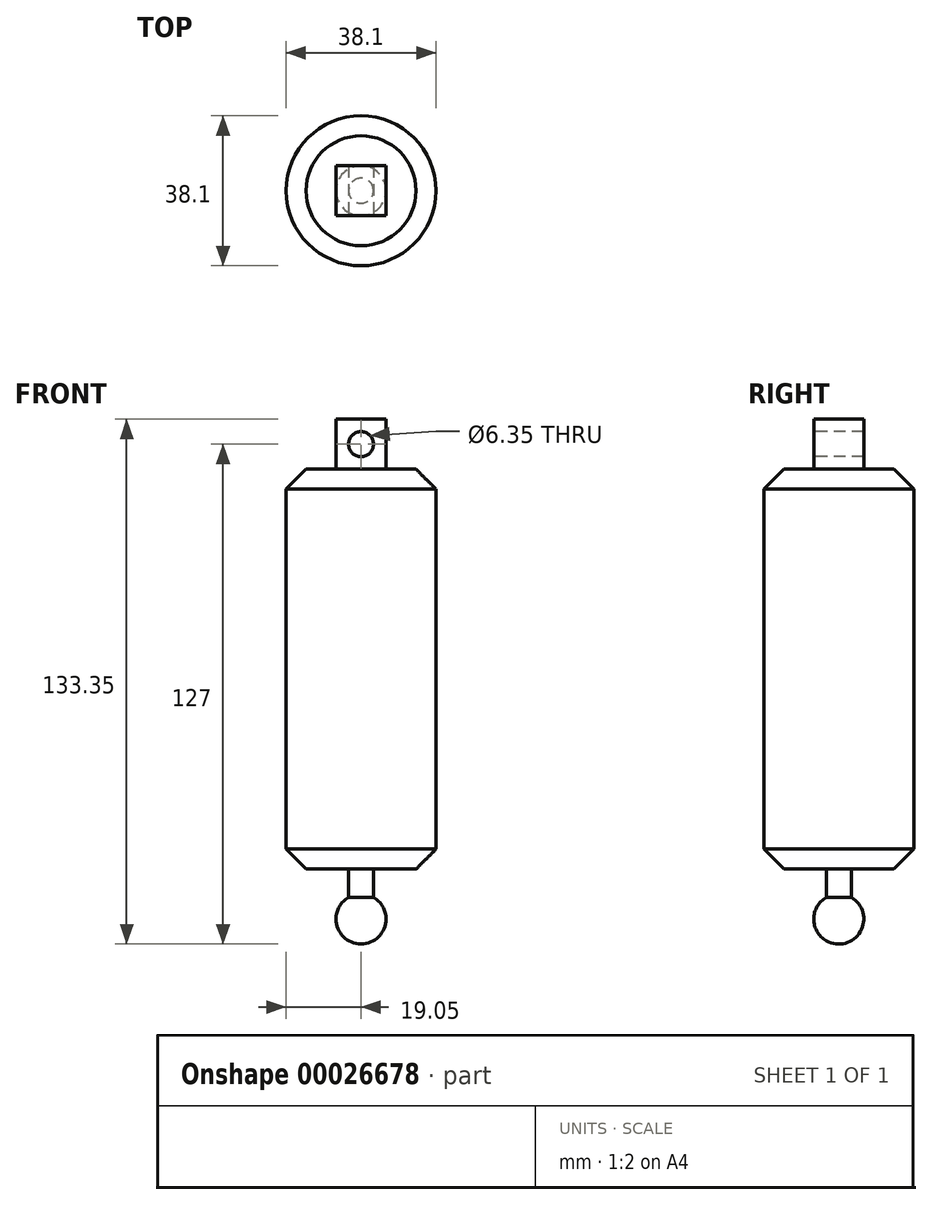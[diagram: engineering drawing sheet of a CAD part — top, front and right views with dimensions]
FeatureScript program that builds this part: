
annotation { "Feature Type Name" : "Feature", "Feature Type Description" : "" }
export const myFeature = defineFeature(function(context is Context, id is Id, definition is map)
    precondition{}
    {
        {
            var Q0;
            Q0=qCreatedBy(makeId("Top.planeOp"),FACE);
            var sketch = newSketch(context, id + "F0", { "sketchPlane" : qUnion([Q0])});
            skCircle(sketch, "E0", {"center": v(0, 0) * mm, "radius": 19.05 * mm});
            skSolve(sketch);
        }
        {
            var Q0;
            Q0=makeQuery(id+"F0.imprint","IMPRINT",FACE,{"disambiguationData":[TD([[makeQuery(id+"F0.imprint","IMPRINT",EDGE,{"derivedFrom":sQuery(id+"F0.wireOp",EDGE,"E0")}),1.0]])]});
            extrude(context, id + "F1", {"entities" : qUnion([Q0]), "depth" : 101.6 * mm});
        }
        {
            var Q0;
            Q0=makeQuery(id+"F1.opExtrude","CAP_EDGE",EDGE,{"disambiguationData":[OSD([sQuery(id+"F0.wireOp",EDGE,"E0")])],"isStart":false});
            var Q1;
            Q1=makeQuery(id+"F1.opExtrude","CAP_EDGE",EDGE,{"disambiguationData":[OSD([sQuery(id+"F0.wireOp",EDGE,"E0")])],"isStart":true});
            chamfer(context, id + "F2", {"entities" : qUnion([Q0, Q1]), "width" : 5.08 * mm, "tangentPropagation" : true});
        }
        {
            var Q0;
            Q0=makeQuery(id+"F1.opExtrude","CAP_FACE",FACE,{"disambiguationData":[OSD([sQuery(id+"F0.wireOp",EDGE,"E0")])],"isStart":true});
            var sketch = newSketch(context, id + "F3", { "sketchPlane" : qUnion([Q0])});
            skCircle(sketch, "E1", {"center": v(0, 0) * mm, "radius": 3.18 * mm});
            skSolve(sketch);
        }
        {
            var Q0;
            Q0=makeQuery(id+"F3.imprint","IMPRINT",FACE,{"disambiguationData":[TD([[makeQuery(id+"F3.imprint","IMPRINT",EDGE,{"derivedFrom":sQuery(id+"F3.wireOp",EDGE,"E1")}),1.0]])]});
            extrude(context, id + "F4", {"entities" : qUnion([Q0]), "operationType" : NewBodyOperationType.ADD, "depth" : 12.7 * mm});
        }
        {
            var Q0;
            Q0=makeQuery(id+"F4.opExtrude","CAP_FACE",FACE,{"disambiguationData":[OSD([sQuery(id+"F3.wireOp",EDGE,"E1")])],"isStart":false});
            var sketch = newSketch(context, id + "F5", { "sketchPlane" : qUnion([Q0])});
            skCircle(sketch, "E2", {"center": v(0, 0) * mm, "radius": 6.35 * mm});
            skLineSegment(sketch, "E3", {"start": v(6.35, 0) * mm, "end": v(-6.35, 0) * mm});
            skSolve(sketch);
        }
        {
            var Q0;
            {var subQ1=sQuery(id+"F5.wireOp",EDGE,"E3");var subQ4=sQuery(id+"F5.wireOp",EDGE,"E2");var subQ6=makeQuery(id+"F5.imprint","INTERSECT",VERTEX,{"disambiguationData":[OD(0.0)],"derivedFrom":[subQ4,subQ1]});Q0=makeQuery(id+"F5.imprint","IMPRINT",FACE,{"disambiguationData":[TD([[makeQuery(id+"F5.imprint","IMPRINT",EDGE,{"disambiguationData":[TD([[subQ6,-1.0]])],"derivedFrom":subQ4}),1.0]])]});}
            var Q1;
            {var subQ0=makeQuery(id+"F4.opExtrude","CAP_EDGE",EDGE,{"disambiguationData":[OSD([sQuery(id+"F3.wireOp",EDGE,"E1")])],"isStart":false});var subQ1=sQuery(id+"F5.wireOp",EDGE,"E3");var subQ3=makeQuery(id+"F5.imprint","INTERSECT",VERTEX,{"disambiguationData":[OD(0.0)],"derivedFrom":[subQ0,subQ1]});Q1=makeQuery(id+"F5.imprint","IMPRINT",FACE,{"disambiguationData":[TD([[makeQuery(id+"F5.imprint","IMPRINT",EDGE,{"disambiguationData":[TD([[subQ3,-1.0]])],"derivedFrom":subQ1}),-1.0]])]});}
            var Q2;
            Q2=sQuery(id+"F5.wireOp",EDGE,"E3");
            revolve(context, id + "F6", {"operationType" : NewBodyOperationType.ADD, "entities" : qUnion([Q0, Q1]), "axis" : qUnion([Q2]), "revolveType" : RevolveType.FULL});
        }
        {
            var Q0;
            Q0=makeQuery(id+"F1.opExtrude","CAP_FACE",FACE,{"disambiguationData":[OSD([sQuery(id+"F0.wireOp",EDGE,"E0")])],"isStart":false});
            var sketch = newSketch(context, id + "F7", { "sketchPlane" : qUnion([Q0])});
            skLineSegment(sketch, "E4.rect.bottom", {"start": v(-6.35, 6.35) * mm, "end": v(6.35, 6.35) * mm});
            skLineSegment(sketch, "E4.rect.top", {"start": v(-6.35, -6.35) * mm, "end": v(6.35, -6.35) * mm});
            skLineSegment(sketch, "E4.rect.left", {"start": v(-6.35, 6.35) * mm, "end": v(-6.35, -6.35) * mm});
            skLineSegment(sketch, "E4.rect.right", {"start": v(6.35, 6.35) * mm, "end": v(6.35, -6.35) * mm});
            skPoint(sketch, "E4.rect.middle", {"position": v(0, 0) * mm});
            skSolve(sketch);
        }
        {
            var Q0;
            Q0=makeQuery(id+"F7.imprint","IMPRINT",FACE,{"disambiguationData":[TD([[makeQuery(id+"F7.imprint","IMPRINT",EDGE,{"derivedFrom":sQuery(id+"F7.wireOp",EDGE,"E4.rect.bottom")}),-1.0]])]});
            extrude(context, id + "F8", {"entities" : qUnion([Q0]), "operationType" : NewBodyOperationType.ADD, "depth" : 12.7 * mm});
        }
        {
            var Q0;
            Q0=makeQuery(id+"F8.opExtrude","SWEPT_FACE",FACE,{"disambiguationData":[OSD([sQuery(id+"F7.wireOp",EDGE,"E4.rect.top")])]});
            var sketch = newSketch(context, id + "F9", { "sketchPlane" : qUnion([Q0])});
            skLineSegment(sketch, "E5", {"start": v(0, 114.3) * mm, "end": v(0, 101.6) * mm});
            skLineSegment(sketch, "E6", {"start": v(-6.35, 107.95) * mm, "end": v(6.35, 107.95) * mm});
            skCircle(sketch, "E7", {"center": v(0, 107.95) * mm, "radius": 3.18 * mm});
            skSolve(sketch);
        }
        {
            var Q0;
            Q0=sQuery(id+"F9.wireOp",VERTEX,"E7.center");
            var Q1;
            Q1=makeQuery(id+"F1.opExtrude","SWEPT_BODY",BODY,{"disambiguationData":[OSD([sQuery(id+"F0.wireOp",EDGE,"E0")])]});
            hole(context, id + "F10", {"style" : HoleStyle.SIMPLE, "holeDiameter" : 6.35 * mm, "endStyle" : HoleEndStyle.THROUGH, "locations" : qUnion([Q0]), "scope" : qUnion([Q1])});
        }
    });
